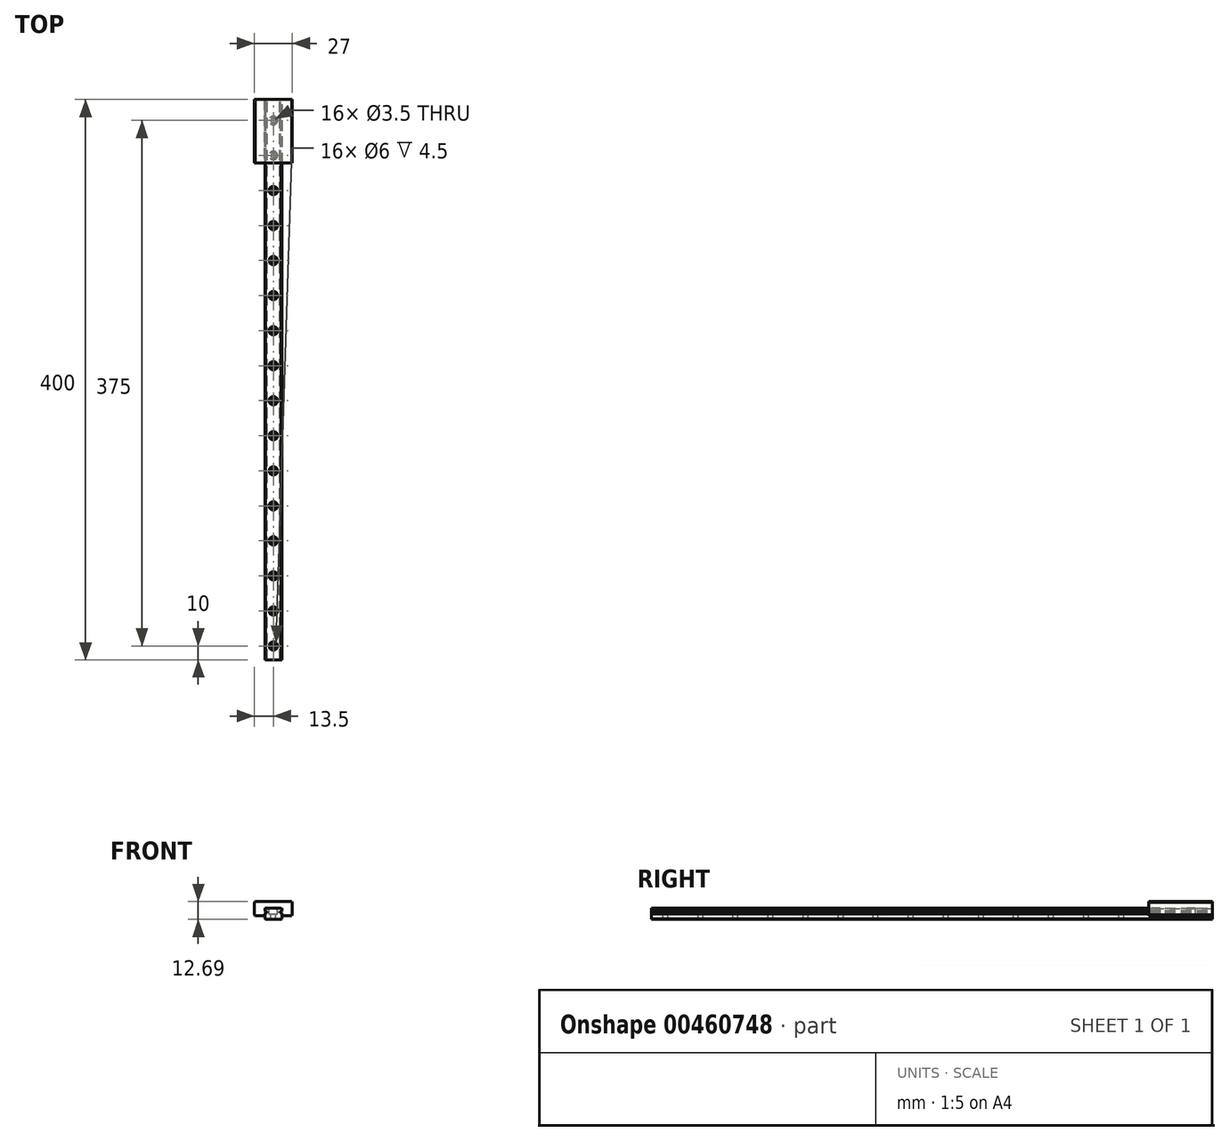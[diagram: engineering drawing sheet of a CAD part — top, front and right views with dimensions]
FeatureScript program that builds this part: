
annotation { "Feature Type Name" : "Feature", "Feature Type Description" : "" }
export const myFeature = defineFeature(function(context is Context, id is Id, definition is map)
    precondition{}
    {
        {
            var Q0;
            Q0=qCreatedBy(makeId("Front.planeOp"),FACE);
            var sketch = newSketch(context, id + "F0", { "sketchPlane" : qUnion([Q0])});
            skLineSegment(sketch, "E0", {"start": v(0, 0) * mm, "end": v(6, 0) * mm});
            skLineSegment(sketch, "E1", {"start": v(6, 0) * mm, "end": v(6, 4) * mm});
            skLineSegment(sketch, "E2", {"start": v(6, 4) * mm, "end": v(5, 5) * mm});
            skLineSegment(sketch, "E3", {"start": v(5, 5) * mm, "end": v(4.5, 5) * mm});
            skLineSegment(sketch, "E4", {"start": v(4.5, 5) * mm, "end": v(4.5, 5.5) * mm});
            skLineSegment(sketch, "E5", {"start": v(4.5, 5.5) * mm, "end": v(5, 5.5) * mm});
            skLineSegment(sketch, "E6", {"start": v(5, 5.5) * mm, "end": v(6, 6.5) * mm});
            skLineSegment(sketch, "E7", {"start": v(6, 6.5) * mm, "end": v(6, 8) * mm});
            skLineSegment(sketch, "E8", {"start": v(6, 8) * mm, "end": v(0, 8) * mm});
            skLineSegment(sketch, "E9.MirrorCS", {"start": v(-4.5, 5) * mm, "end": v(-4.5, 5.5) * mm});
            skLineSegment(sketch, "E10.MirrorCS", {"start": v(-4.5, 5.5) * mm, "end": v(-5, 5.5) * mm});
            skLineSegment(sketch, "E11.MirrorCS", {"start": v(-5, 5) * mm, "end": v(-4.5, 5) * mm});
            skLineSegment(sketch, "E12.MirrorCS", {"start": v(0, 0) * mm, "end": v(-6, 0) * mm});
            skLineSegment(sketch, "E13.MirrorCS", {"start": v(-6, 0) * mm, "end": v(-6, 4) * mm});
            skLineSegment(sketch, "E14.MirrorCS", {"start": v(-6, 8) * mm, "end": v(0, 8) * mm});
            skLineSegment(sketch, "E15.MirrorCS", {"start": v(-5, 5.5) * mm, "end": v(-6, 6.5) * mm});
            skLineSegment(sketch, "E16.MirrorCS", {"start": v(-6, 6.5) * mm, "end": v(-6, 8) * mm});
            skLineSegment(sketch, "E17.MirrorCS", {"start": v(-6, 4) * mm, "end": v(-5, 5) * mm});
            skSolve(sketch);
        }
        {
            var Q0;
            Q0=makeQuery(id+"F0.imprint","IMPRINT",FACE,{"disambiguationData":[TD([[makeQuery(id+"F0.imprint","IMPRINT",EDGE,{"derivedFrom":sQuery(id+"F0.wireOp",EDGE,"E0")}),1.0]])]});
            extrude(context, id + "F1", {"entities" : qUnion([Q0]), "depth" : 400 * mm, "offsetDistance" : 25 * mm});
        }
        {
            var Q0;
            Q0=makeQuery(id+"F1.opExtrude","SWEPT_EDGE",EDGE,{"disambiguationData":[OSD([sQuery(id+"F0.wireOp",EDGE,"E7"),sQuery(id+"F0.wireOp",EDGE,"E8")])]});
            var Q1;
            Q1=makeQuery(id+"F1.opExtrude","SWEPT_EDGE",EDGE,{"disambiguationData":[OSD([sQuery(id+"F0.wireOp",EDGE,"E14.MirrorCS"),sQuery(id+"F0.wireOp",EDGE,"E16.MirrorCS")])]});
            var Q2;
            Q2=makeQuery(id+"F1.opExtrude","SWEPT_EDGE",EDGE,{"disambiguationData":[OSD([sQuery(id+"F0.wireOp",EDGE,"E0"),sQuery(id+"F0.wireOp",EDGE,"E1")])]});
            var Q3;
            Q3=makeQuery(id+"F1.opExtrude","SWEPT_EDGE",EDGE,{"disambiguationData":[OSD([sQuery(id+"F0.wireOp",EDGE,"E12.MirrorCS"),sQuery(id+"F0.wireOp",EDGE,"E13.MirrorCS")])]});
            chamfer(context, id + "F2", {"entities" : qUnion([Q0, Q1, Q2, Q3]), "width" : 0.5 * mm, "tangentPropagation" : true});
        }
        {
            var Q0;
            Q0=makeQuery(id+"F1.opExtrude","SWEPT_FACE",FACE,{"disambiguationData":[OSD([sQuery(id+"F0.wireOp",EDGE,"E8"),sQuery(id+"F0.wireOp",EDGE,"E14.MirrorCS")])]});
            var sketch = newSketch(context, id + "F3", { "sketchPlane" : qUnion([Q0])});
            skPoint(sketch, "E18", {"position": v(0, -390) * mm});
            skPoint(sketch, "E18.positionSnap0", {"position": v(0, -400) * mm});
            skPoint(sketch, "E19.0.1.0", {"position": v(0, -365) * mm});
            skPoint(sketch, "E19.0.2.0", {"position": v(0, -340) * mm});
            skPoint(sketch, "E19.0.3.0", {"position": v(0, -315) * mm});
            skPoint(sketch, "E19.0.4.0", {"position": v(0, -290) * mm});
            skPoint(sketch, "E19.0.5.0", {"position": v(0, -265) * mm});
            skPoint(sketch, "E19.0.6.0", {"position": v(0, -240) * mm});
            skPoint(sketch, "E19.0.7.0", {"position": v(0, -215) * mm});
            skPoint(sketch, "E19.0.8.0", {"position": v(0, -190) * mm});
            skPoint(sketch, "E19.0.9.0", {"position": v(0, -165) * mm});
            skPoint(sketch, "E19.0.10.0", {"position": v(0, -140) * mm});
            skPoint(sketch, "E19.0.11.0", {"position": v(0, -115) * mm});
            skPoint(sketch, "E19.0.12.0", {"position": v(0, -90) * mm});
            skPoint(sketch, "E19.0.13.0", {"position": v(0, -65) * mm});
            skPoint(sketch, "E19.0.14.0", {"position": v(0, -40) * mm});
            skPoint(sketch, "E19.0.15.0", {"position": v(0, -15) * mm});
            skLineSegment(sketch, "E19.direction1", {"start": v(0, -390) * mm, "end": v(25, -390) * mm, "construction": true});
            skLineSegment(sketch, "E19.direction2", {"start": v(0, -390) * mm, "end": v(0, -365) * mm, "construction": true});
            skSolve(sketch);
        }
        {
            var Q0;
            Q0=sQuery(id+"F3.wireOp",VERTEX,"E18");
            var Q1;
            Q1=sQuery(id+"F3.wireOp",VERTEX,"E19.0.1.0");
            var Q2;
            Q2=sQuery(id+"F3.wireOp",VERTEX,"E19.0.2.0");
            var Q3;
            Q3=sQuery(id+"F3.wireOp",VERTEX,"E19.0.3.0");
            var Q4;
            Q4=sQuery(id+"F3.wireOp",VERTEX,"E19.0.4.0");
            var Q5;
            Q5=sQuery(id+"F3.wireOp",VERTEX,"E19.0.5.0");
            var Q6;
            Q6=sQuery(id+"F3.wireOp",VERTEX,"E19.0.6.0");
            var Q7;
            Q7=sQuery(id+"F3.wireOp",VERTEX,"E19.0.7.0");
            var Q8;
            Q8=sQuery(id+"F3.wireOp",VERTEX,"E19.0.8.0");
            var Q9;
            Q9=sQuery(id+"F3.wireOp",VERTEX,"E19.0.9.0");
            var Q10;
            Q10=sQuery(id+"F3.wireOp",VERTEX,"E19.0.11.0");
            var Q11;
            Q11=sQuery(id+"F3.wireOp",VERTEX,"E19.0.10.0");
            var Q12;
            Q12=sQuery(id+"F3.wireOp",VERTEX,"E19.0.12.0");
            var Q13;
            Q13=sQuery(id+"F3.wireOp",VERTEX,"E19.0.13.0");
            var Q14;
            Q14=sQuery(id+"F3.wireOp",VERTEX,"E19.0.14.0");
            var Q15;
            Q15=sQuery(id+"F3.wireOp",VERTEX,"E19.0.15.0");
            var Q16;
            Q16=makeQuery(id+"F1.opExtrude","SWEPT_BODY",BODY,{"disambiguationData":[OSD([sQuery(id+"F0.wireOp",EDGE,"E0"),sQuery(id+"F0.wireOp",EDGE,"E1"),sQuery(id+"F0.wireOp",EDGE,"E2"),sQuery(id+"F0.wireOp",EDGE,"E3"),sQuery(id+"F0.wireOp",EDGE,"E4"),sQuery(id+"F0.wireOp",EDGE,"E5"),sQuery(id+"F0.wireOp",EDGE,"E6"),sQuery(id+"F0.wireOp",EDGE,"E7"),sQuery(id+"F0.wireOp",EDGE,"E8"),sQuery(id+"F0.wireOp",EDGE,"E9.MirrorCS"),sQuery(id+"F0.wireOp",EDGE,"E10.MirrorCS"),sQuery(id+"F0.wireOp",EDGE,"E11.MirrorCS"),sQuery(id+"F0.wireOp",EDGE,"E12.MirrorCS"),sQuery(id+"F0.wireOp",EDGE,"E13.MirrorCS"),sQuery(id+"F0.wireOp",EDGE,"E14.MirrorCS"),sQuery(id+"F0.wireOp",EDGE,"E15.MirrorCS"),sQuery(id+"F0.wireOp",EDGE,"E16.MirrorCS"),sQuery(id+"F0.wireOp",EDGE,"E17.MirrorCS")])]});
            hole(context, id + "F4", {"style" : HoleStyle.C_BORE, "endStyle" : HoleEndStyle.THROUGH, "holeDiameter" : 3.5 * mm, "cBoreDiameter" : 6 * mm, "cBoreDepth" : 4.5 * mm, "isTappedThrough" : true, "tappedDepth" : 12 * mm, "tapClearance" : 3, "locations" : qUnion([Q0, Q1, Q2, Q3, Q4, Q5, Q6, Q7, Q8, Q9, Q10, Q11, Q12, Q13, Q14, Q15]), "scope" : qUnion([Q16])});
        }
        {
            var Q0;
            Q0=qCreatedBy(makeId("Front.planeOp"),FACE);
            var sketch = newSketch(context, id + "F5", { "sketchPlane" : qUnion([Q0])});
            skLineSegment(sketch, "E20", {"start": v(0, 12.69) * mm, "end": v(13.5, 12.69) * mm});
            skLineSegment(sketch, "E21", {"start": v(13.5, 12.69) * mm, "end": v(13.5, 2.69) * mm});
            skLineSegment(sketch, "E22", {"start": v(13.5, 2.69) * mm, "end": v(6, 2.69) * mm});
            skLineSegment(sketch, "E23", {"start": v(6, 2.69) * mm, "end": v(6, 4.28) * mm});
            skLineSegment(sketch, "E24", {"start": v(6, 4.28) * mm, "end": v(5.3, 4.98) * mm});
            skLineSegment(sketch, "E25", {"start": v(5.3, 4.98) * mm, "end": v(5.3, 5.48) * mm});
            skLineSegment(sketch, "E26", {"start": v(5.3, 5.48) * mm, "end": v(6, 6.18) * mm});
            skLineSegment(sketch, "E27", {"start": v(6, 6.18) * mm, "end": v(6, 8) * mm});
            skLineSegment(sketch, "E28", {"start": v(6, 8) * mm, "end": v(0, 8) * mm});
            skPoint(sketch, "E29", {"position": v(5.3, 5.23) * mm});
            skLineSegment(sketch, "E30.MirrorCS", {"start": v(0, 12.69) * mm, "end": v(-13.5, 12.69) * mm});
            skLineSegment(sketch, "E31.MirrorCS", {"start": v(-13.5, 12.69) * mm, "end": v(-13.5, 2.69) * mm});
            skLineSegment(sketch, "E32.MirrorCS", {"start": v(-13.5, 2.69) * mm, "end": v(-6, 2.69) * mm});
            skLineSegment(sketch, "E33.MirrorCS", {"start": v(-6, 2.69) * mm, "end": v(-6, 4.28) * mm});
            skLineSegment(sketch, "E34.MirrorCS", {"start": v(-6, 4.28) * mm, "end": v(-5.3, 4.98) * mm});
            skLineSegment(sketch, "E35.MirrorCS", {"start": v(-5.3, 4.98) * mm, "end": v(-5.3, 5.48) * mm});
            skLineSegment(sketch, "E36.MirrorCS", {"start": v(-5.3, 5.48) * mm, "end": v(-6, 6.18) * mm});
            skLineSegment(sketch, "E37.MirrorCS", {"start": v(-6, 6.18) * mm, "end": v(-6, 8) * mm});
            skLineSegment(sketch, "E38.MirrorCS", {"start": v(-6, 8) * mm, "end": v(0, 8) * mm});
            skSolve(sketch);
        }
        {
            var Q0;
            Q0=makeQuery(id+"F5.imprint","IMPRINT",FACE,{"disambiguationData":[TD([[makeQuery(id+"F5.imprint","IMPRINT",EDGE,{"derivedFrom":sQuery(id+"F5.wireOp",EDGE,"E20")}),-1.0]])]});
            extrude(context, id + "F6", {"entities" : qUnion([Q0]), "depth" : 45.4 * mm});
        }
        {
            var Q0;
            Q0=makeQuery(id+"F6.opExtrude","SWEPT_EDGE",EDGE,{"disambiguationData":[OSD([sQuery(id+"F5.wireOp",EDGE,"E21"),sQuery(id+"F5.wireOp",EDGE,"E22")])]});
            var Q1;
            Q1=makeQuery(id+"F6.opExtrude","SWEPT_EDGE",EDGE,{"disambiguationData":[OSD([sQuery(id+"F5.wireOp",EDGE,"E20"),sQuery(id+"F5.wireOp",EDGE,"E21")])]});
            var Q2;
            Q2=makeQuery(id+"F6.opExtrude","SWEPT_EDGE",EDGE,{"disambiguationData":[OSD([sQuery(id+"F5.wireOp",EDGE,"E30.MirrorCS"),sQuery(id+"F5.wireOp",EDGE,"E31.MirrorCS")])]});
            var Q3;
            Q3=makeQuery(id+"F6.opExtrude","SWEPT_EDGE",EDGE,{"disambiguationData":[OSD([sQuery(id+"F5.wireOp",EDGE,"E31.MirrorCS"),sQuery(id+"F5.wireOp",EDGE,"E32.MirrorCS")])]});
            var Q4;
            Q4=makeQuery(id+"F6.opExtrude","SWEPT_EDGE",EDGE,{"disambiguationData":[OSD([sQuery(id+"F5.wireOp",EDGE,"E32.MirrorCS"),sQuery(id+"F5.wireOp",EDGE,"E33.MirrorCS")])]});
            var Q5;
            Q5=makeQuery(id+"F6.opExtrude","SWEPT_EDGE",EDGE,{"disambiguationData":[OSD([sQuery(id+"F5.wireOp",EDGE,"E22"),sQuery(id+"F5.wireOp",EDGE,"E23")])]});
            chamfer(context, id + "F7", {"entities" : qUnion([Q0, Q1, Q2, Q3, Q4, Q5]), "width" : 0.5 * mm, "tangentPropagation" : true});
        }
    });
